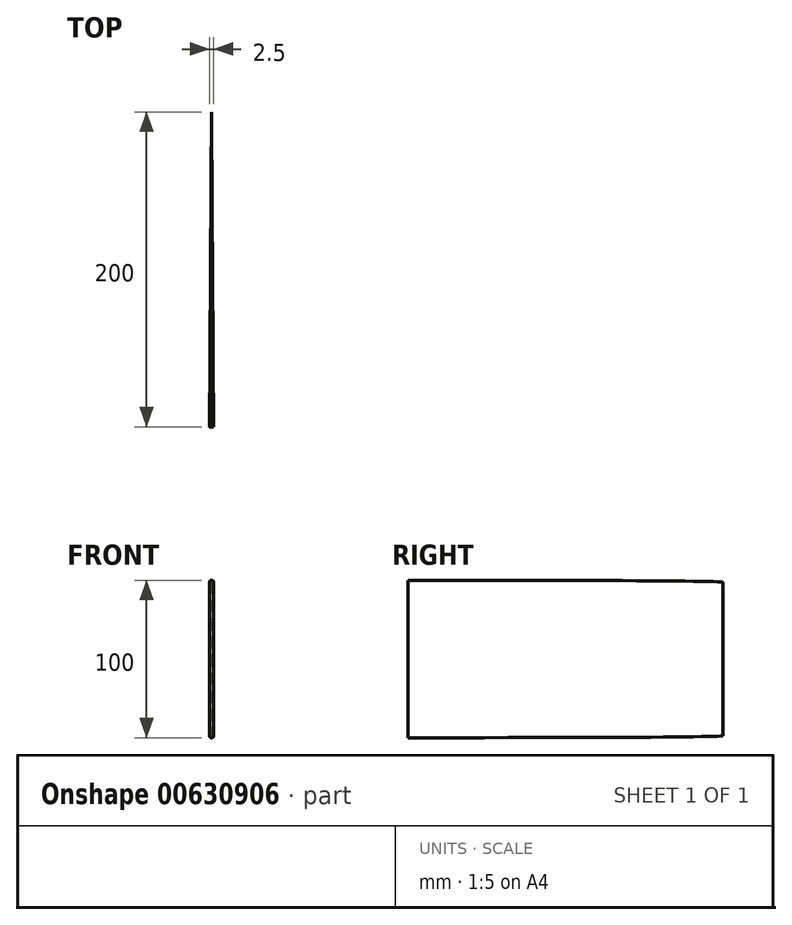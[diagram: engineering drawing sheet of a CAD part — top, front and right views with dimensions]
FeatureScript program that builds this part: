
annotation { "Feature Type Name" : "Feature", "Feature Type Description" : "" }
export const myFeature = defineFeature(function(context is Context, id is Id, definition is map)
    precondition{}
    {
        {
            var Q0;
            Q0=qCreatedBy(makeId("Top.planeOp"),FACE);
            var sketch = newSketch(context, id + "F0", { "sketchPlane" : qUnion([Q0])});
            skLineSegment(sketch, "E0", {"start": v(0, 0) * mm, "end": v(1.25, 0) * mm});
            skLineSegment(sketch, "E1", {"start": v(0, 0) * mm, "end": v(-1.25, 0) * mm});
            skLineSegment(sketch, "E2", {"start": v(0, 0) * mm, "end": v(0, 200) * mm});
            skLineSegment(sketch, "E3", {"start": v(1.25, 0) * mm, "end": v(0, 200) * mm});
            skLineSegment(sketch, "E4", {"start": v(-1.25, 0) * mm, "end": v(0, 200) * mm});
            skSolve(sketch);
        }
        {
            var Q0;
            Q0 = qSketchRegion(id + "F0", true);
            extrude(context, id + "F1", {"entities" : qUnion([Q0]), "endBound" : BoundingType.SYMMETRIC, "depth" : 100 * mm, "offsetDistance" : 25 * mm});
        }
        {
            var Q0;
            Q0=makeQuery(id+"F1.opExtrude","CAP_EDGE",EDGE,{"disambiguationData":[OSD([sQuery(id+"F0.wireOp",EDGE,"E4")])],"isStart":false});
            var Q1;
            Q1=makeQuery(id+"F1.opExtrude","CAP_EDGE",EDGE,{"disambiguationData":[OSD([sQuery(id+"F0.wireOp",EDGE,"E3")])],"isStart":false});
            var Q2;
            Q2=makeQuery(id+"F1.opExtrude","CAP_EDGE",EDGE,{"disambiguationData":[OSD([sQuery(id+"F0.wireOp",EDGE,"E4")])],"isStart":true});
            var Q3;
            Q3=makeQuery(id+"F1.opExtrude","CAP_EDGE",EDGE,{"disambiguationData":[OSD([sQuery(id+"F0.wireOp",EDGE,"E3")])],"isStart":true});
            fillet(context, id + "F2", {"entities" : qUnion([Q0, Q1, Q2, Q3]), "radius" : 1.25 * mm, "rho" : 0.5, "crossSection" : FilletCrossSection.CONIC, "allowEdgeOverflow" : false});
        }
    });
